# Revit family: Gira_2282600
name_source: partatom
category: Electrical Fixtures
revit_build: Autodesk Revit 2017 (Build: 20160225_1515(x64)
units: mm (PartAtom-declared; Revit-internal decimal feet)

## family parameters
Cut with Voids When Loaded = No
Host = Face
Maintain Annotation Orientation = Yes
Part Type = Normal
Room Calculation Point = No
Round Connector Dimension = Use Diameter
Shared = No

## types (1)
- Speaker RDS FM radio System 55 stainl.steel
    Available = No
    BIM (1) = https://media.stage.bim.site und Tasten.rfa?public/gira/36a6b08/Sys55_Komplettgerät_Schalten und Tasten.rfa
    Category = Electronic insert for domestic switching devices
    Data sheet (1) = https://katalog.gira.de
    Default Elevation = 1219 mm
    Description = Spk.FM radio RDS Sys55 SST,Speaker for the RDS flush-mounted radio,,Stainless steel,Features:,- Speaker for connection to the Gira RDS flush-mounted radio.
    GTIN = 4010337032861
    HAN = 2282600
    HeinzeBIM = https://bimportal.heinze.de
    Manufacturer = Gira
    Manufacturer URL = https://www.gira.de
    Model = Radio
    Name = Speaker RDS FM radio System 55 stainl.steel
    URL = http://katalog.gira.de

## geometry (parser evidence)
native form markers: Blend x2, Sweep x10
no freeform markers — native parametric forms only
